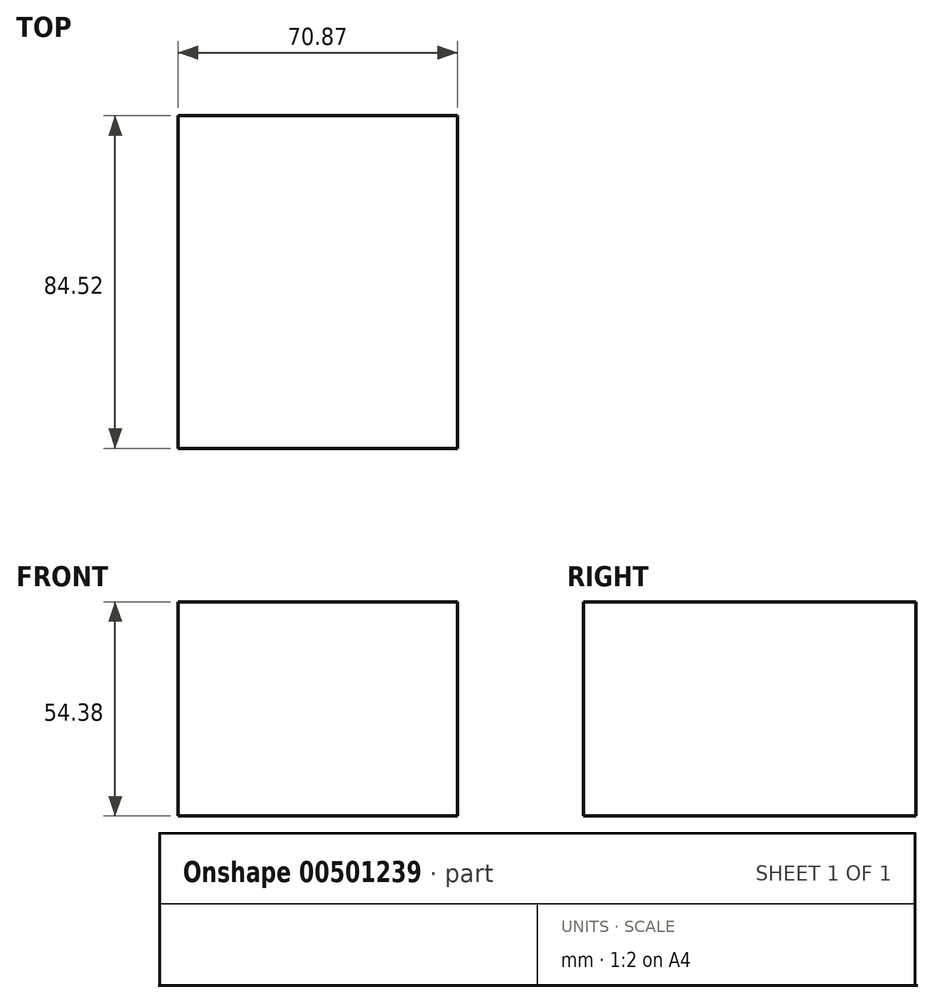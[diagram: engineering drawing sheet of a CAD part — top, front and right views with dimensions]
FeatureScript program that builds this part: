
annotation { "Feature Type Name" : "Feature", "Feature Type Description" : "" }
export const myFeature = defineFeature(function(context is Context, id is Id, definition is map)
    precondition{}
    {
        {
            var Q0;
            Q0=qCreatedBy(makeId("Right.planeOp"),FACE);
            var sketch = newSketch(context, id + "F0", { "sketchPlane" : qUnion([Q0])});
            skLineSegment(sketch, "E0.bottom", {"start": v(-42.26, 27.19) * mm, "end": v(42.26, 27.19) * mm});
            skLineSegment(sketch, "E0.top", {"start": v(-42.26, -27.19) * mm, "end": v(42.26, -27.19) * mm});
            skLineSegment(sketch, "E0.left", {"start": v(-42.26, 27.19) * mm, "end": v(-42.26, -27.19) * mm});
            skLineSegment(sketch, "E0.right", {"start": v(42.26, 27.19) * mm, "end": v(42.26, -27.19) * mm});
            skPoint(sketch, "E0.middle", {"position": v(0, 0) * mm});
            skSolve(sketch);
        }
        {
            var Q0;
            Q0 = qSketchRegion(id + "F0", true);
            extrude(context, id + "F1", {"entities" : qUnion([Q0]), "depth" : 70.87 * mm});
        }
    });
